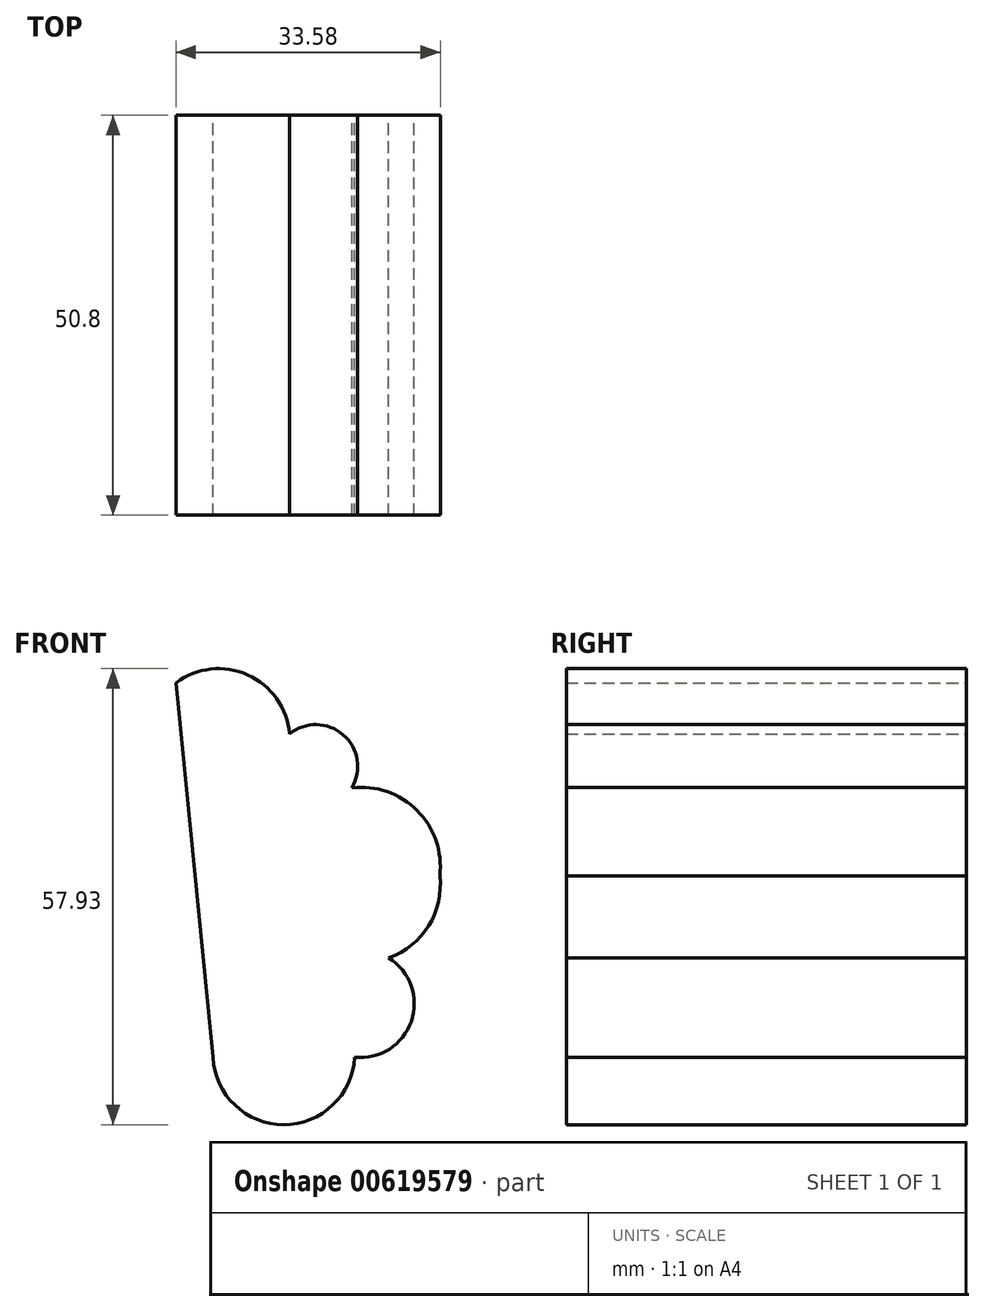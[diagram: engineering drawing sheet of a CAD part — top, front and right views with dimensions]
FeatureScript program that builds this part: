
annotation { "Feature Type Name" : "Feature", "Feature Type Description" : "" }
export const myFeature = defineFeature(function(context is Context, id is Id, definition is map)
    precondition{}
    {
        {
            var Q0;
            Q0=qCreatedBy(makeId("Front.planeOp"),FACE);
            var sketch = newSketch(context, id + "F0", { "sketchPlane" : qUnion([Q0])});
            skArc(sketch, "E0", {"start": v(26.84, 36.2) * mm, "mid": v(21.55, 43.7) * mm, "end": v(12.43, 42.7) * mm});
            skArc(sketch, "E1", {"start": v(34.77, 29.36) * mm, "mid": v(33.67, 36.1) * mm, "end": v(26.84, 36.2) * mm});
            skArc(sketch, "E2", {"start": v(45.94, 18.2) * mm, "mid": v(43.06, 26.49) * mm, "end": v(34.77, 29.36) * mm});
            skArc(sketch, "E3", {"start": v(39.45, 7.75) * mm, "mid": v(44.53, 11.83) * mm, "end": v(45.94, 18.2) * mm});
            skArc(sketch, "E4", {"start": v(35.13, -4.86) * mm, "mid": v(42.33, -0.29) * mm, "end": v(39.45, 7.75) * mm});
            skArc(sketch, "E5", {"start": v(17.11, -4.86) * mm, "mid": v(26.12, -13.43) * mm, "end": v(35.13, -4.86) * mm});
            skLineSegment(sketch, "E6", {"start": v(12.43, 42.7) * mm, "end": v(17.11, -4.86) * mm});
            skLineSegment(sketch, "E7", {"start": v(26.84, 36.2) * mm, "end": v(35.13, -4.86) * mm});
            skSolve(sketch);
        }
        {
            var Q0;
            Q0 = qSketchRegion(id + "F0", true);
            extrude(context, id + "F1", {"entities" : qUnion([Q0]), "endBound" : BoundingType.SYMMETRIC, "depth" : 50.8 * mm, "offsetDistance" : 25.4 * mm});
        }
    });
